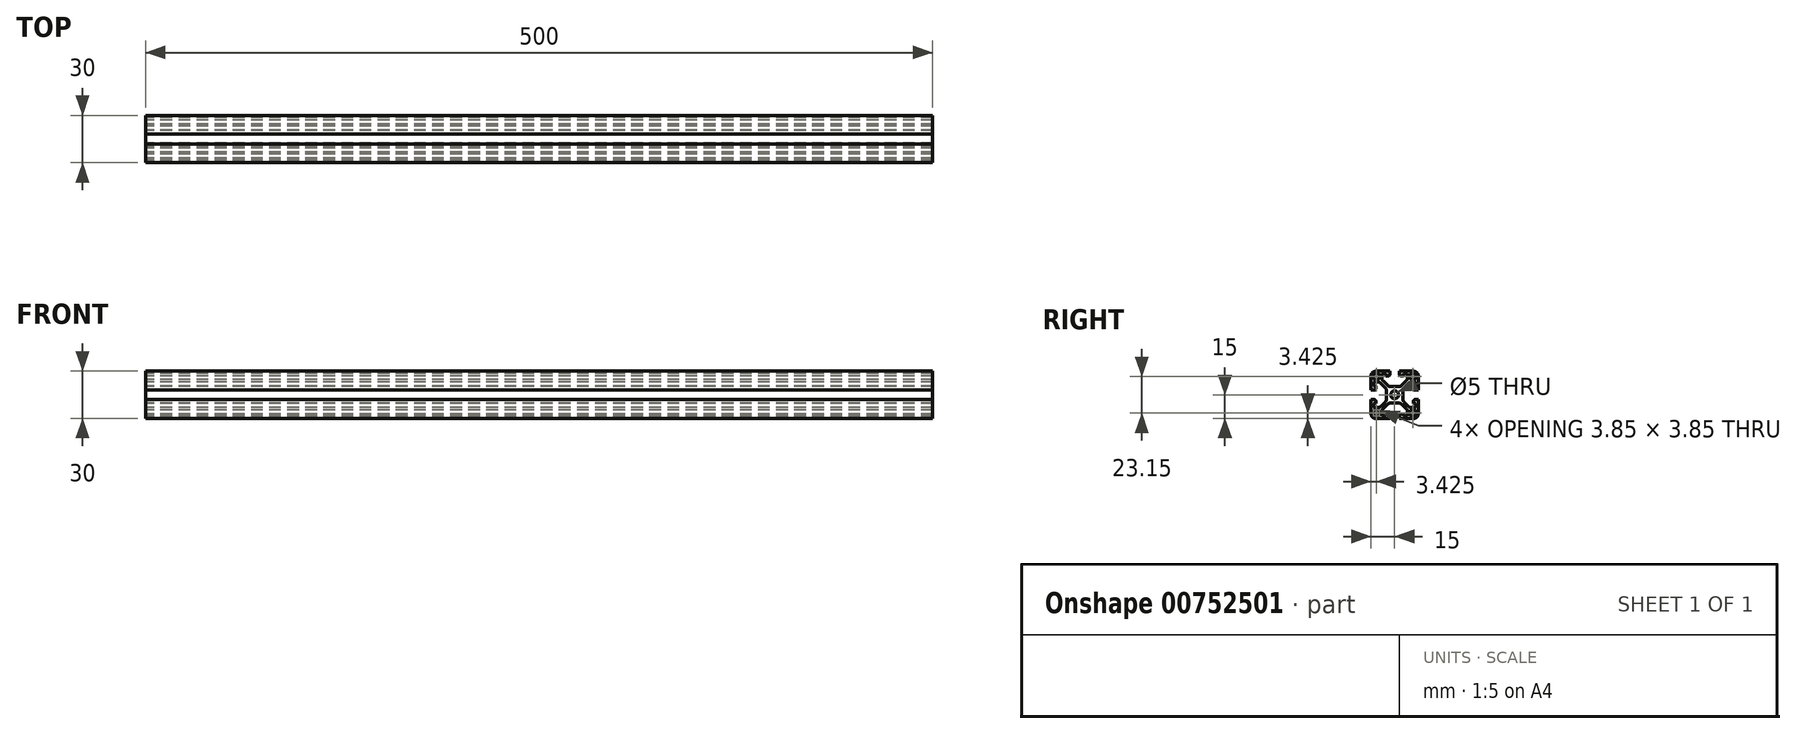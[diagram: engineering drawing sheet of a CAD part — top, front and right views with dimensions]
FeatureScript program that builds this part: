
annotation { "Feature Type Name" : "Feature", "Feature Type Description" : "" }
export const myFeature = defineFeature(function(context is Context, id is Id, definition is map)
    precondition{}
    {
        {
            var Q0;
            Q0=qCreatedBy(makeId("Right.planeOp"),FACE);
            var sketch = newSketch(context, id + "F0", { "sketchPlane" : qUnion([Q0])});
            skLineSegment(sketch, "E0.bottom", {"start": v(-12, 15) * mm, "end": v(-3.1, 15) * mm});
            skLineSegment(sketch, "E0.top", {"start": v(-12, -15) * mm, "end": v(-3.1, -15) * mm});
            skLineSegment(sketch, "E0.right", {"start": v(15, 12) * mm, "end": v(15, 3.1) * mm});
            skLineSegment(sketch, "E1", {"start": v(0, 31.7) * mm, "end": v(0, -24.01) * mm, "construction": true});
            skLineSegment(sketch, "E2", {"start": v(-29.71, 0) * mm, "end": v(21.95, 0) * mm, "construction": true});
            skLineSegment(sketch, "E3", {"start": v(-3.1, 15) * mm, "end": v(-3.1, 12.8) * mm});
            skLineSegment(sketch, "E4", {"start": v(-3.9, 12) * mm, "end": v(-5.6, 12) * mm});
            skLineSegment(sketch, "E5", {"start": v(-5.6, 12) * mm, "end": v(-5.6, 13.5) * mm});
            skLineSegment(sketch, "E6", {"start": v(-5.6, 13.5) * mm, "end": v(-8.15, 13.5) * mm});
            skLineSegment(sketch, "E7", {"start": v(-8.15, 13.5) * mm, "end": v(-8.15, 10.8) * mm});
            skLineSegment(sketch, "E8", {"start": v(-7.27, 8.68) * mm, "end": v(-4.72, 6.13) * mm});
            skLineSegment(sketch, "E9", {"start": v(-2.6, 5.25) * mm, "end": v(2.6, 5.25) * mm});
            skLineSegment(sketch, "E10", {"start": v(4.72, 6.13) * mm, "end": v(7.27, 8.68) * mm});
            skLineSegment(sketch, "E11", {"start": v(8.15, 10.8) * mm, "end": v(8.15, 13.5) * mm});
            skLineSegment(sketch, "E12", {"start": v(8.15, 13.5) * mm, "end": v(5.6, 13.5) * mm});
            skLineSegment(sketch, "E13", {"start": v(5.6, 13.5) * mm, "end": v(5.6, 12) * mm});
            skLineSegment(sketch, "E14", {"start": v(5.6, 12) * mm, "end": v(3.9, 12) * mm});
            skLineSegment(sketch, "E15", {"start": v(3.1, 12.8) * mm, "end": v(3.1, 15) * mm});
            skLineSegment(sketch, "E16.trimOffspring", {"start": v(3.1, 15) * mm, "end": v(12, 15) * mm});
            skLineSegment(sketch, "E17.bottom", {"start": v(-12, 13.5) * mm, "end": v(-9.65, 13.5) * mm});
            skLineSegment(sketch, "E17.top", {"start": v(-13.5, 9.65) * mm, "end": v(-9.65, 9.65) * mm});
            skLineSegment(sketch, "E17.left", {"start": v(-13.5, 12) * mm, "end": v(-13.5, 9.65) * mm});
            skLineSegment(sketch, "E17.right", {"start": v(-9.65, 13.5) * mm, "end": v(-9.65, 9.65) * mm});
            skPoint(sketch, "E18.visualSharp", {"position": v(-13.5, 13.5) * mm});
            skArc(sketch, "E18.filletArc", {"start": v(-12, 13.5) * mm, "mid": v(-13.06, 13.06) * mm, "end": v(-13.5, 12) * mm});
            skPoint(sketch, "E19.visualSharp", {"position": v(-15, 15) * mm});
            skArc(sketch, "E19.filletArc", {"start": v(-12, 15) * mm, "mid": v(-14.12, 14.12) * mm, "end": v(-15, 12) * mm});
            skPoint(sketch, "E20.visualSharp", {"position": v(-15, -15) * mm});
            skArc(sketch, "E20.filletArc", {"start": v(-15, -12) * mm, "mid": v(-14.12, -14.12) * mm, "end": v(-12, -15) * mm});
            skPoint(sketch, "E21.visualSharp", {"position": v(15, -15) * mm});
            skArc(sketch, "E21.filletArc", {"start": v(12, -15) * mm, "mid": v(14.12, -14.12) * mm, "end": v(15, -12) * mm});
            skPoint(sketch, "E22.visualSharp", {"position": v(15, 15) * mm});
            skArc(sketch, "E22.filletArc", {"start": v(15, 12) * mm, "mid": v(14.12, 14.12) * mm, "end": v(12, 15) * mm});
            skPoint(sketch, "E23.visualSharp", {"position": v(-8.15, 9.56) * mm});
            skArc(sketch, "E23.filletArc", {"start": v(-8.15, 10.8) * mm, "mid": v(-7.92, 9.66) * mm, "end": v(-7.27, 8.68) * mm});
            skPoint(sketch, "E24.visualSharp", {"position": v(-3.84, 5.25) * mm});
            skArc(sketch, "E24.filletArc", {"start": v(-4.72, 6.13) * mm, "mid": v(-3.74, 5.48) * mm, "end": v(-2.6, 5.25) * mm});
            skPoint(sketch, "E25.visualSharp", {"position": v(3.84, 5.25) * mm});
            skArc(sketch, "E25.filletArc", {"start": v(2.6, 5.25) * mm, "mid": v(3.74, 5.48) * mm, "end": v(4.72, 6.13) * mm});
            skPoint(sketch, "E26.visualSharp", {"position": v(8.15, 9.56) * mm});
            skArc(sketch, "E26.filletArc", {"start": v(7.27, 8.68) * mm, "mid": v(7.92, 9.66) * mm, "end": v(8.15, 10.8) * mm});
            skPoint(sketch, "E27.visualSharp", {"position": v(3.1, 12) * mm});
            skArc(sketch, "E27.filletArc", {"start": v(3.1, 12.8) * mm, "mid": v(3.33, 12.23) * mm, "end": v(3.9, 12) * mm});
            skPoint(sketch, "E28.visualSharp", {"position": v(-3.1, 12) * mm});
            skArc(sketch, "E28.filletArc", {"start": v(-3.9, 12) * mm, "mid": v(-3.33, 12.23) * mm, "end": v(-3.1, 12.8) * mm});
            skLineSegment(sketch, "E29.1.0", {"start": v(-5.25, -2.6) * mm, "end": v(-5.25, 2.6) * mm});
            skLineSegment(sketch, "E29.1.1", {"start": v(-12.8, 3.1) * mm, "end": v(-15, 3.1) * mm});
            skLineSegment(sketch, "E29.1.2", {"start": v(-6.13, 4.72) * mm, "end": v(-8.68, 7.27) * mm});
            skPoint(sketch, "E29.1.3", {"position": v(-12, -3.1) * mm});
            skLineSegment(sketch, "E29.1.4", {"start": v(-13.5, -5.6) * mm, "end": v(-13.5, -8.15) * mm});
            skPoint(sketch, "E29.1.5", {"position": v(-5.25, 3.84) * mm});
            skLineSegment(sketch, "E29.1.6", {"start": v(-13.5, -12) * mm, "end": v(-13.5, -9.65) * mm});
            skPoint(sketch, "E29.1.7", {"position": v(-5.25, -3.84) * mm});
            skLineSegment(sketch, "E29.1.8", {"start": v(-10.8, 8.15) * mm, "end": v(-13.5, 8.15) * mm});
            skLineSegment(sketch, "E29.1.9", {"start": v(-9.65, -13.5) * mm, "end": v(-9.65, -9.65) * mm});
            skLineSegment(sketch, "E29.1.10", {"start": v(-12, -13.5) * mm, "end": v(-9.65, -13.5) * mm});
            skLineSegment(sketch, "E29.1.11", {"start": v(-13.5, -8.15) * mm, "end": v(-10.8, -8.15) * mm});
            skLineSegment(sketch, "E29.1.12", {"start": v(-13.5, -9.65) * mm, "end": v(-9.65, -9.65) * mm});
            skPoint(sketch, "E29.1.13", {"position": v(-9.56, 8.15) * mm});
            skLineSegment(sketch, "E29.1.14", {"start": v(-8.68, -7.27) * mm, "end": v(-6.13, -4.72) * mm});
            skPoint(sketch, "E29.1.15", {"position": v(-12, 3.1) * mm});
            skPoint(sketch, "E29.1.16", {"position": v(-9.56, -8.15) * mm});
            skLineSegment(sketch, "E29.1.17", {"start": v(-15, -3.1) * mm, "end": v(-12.8, -3.1) * mm});
            skLineSegment(sketch, "E29.1.18", {"start": v(-13.5, 8.15) * mm, "end": v(-13.5, 5.6) * mm});
            skArc(sketch, "E29.1.19", {"start": v(-10.8, -8.15) * mm, "mid": v(-9.66, -7.92) * mm, "end": v(-8.68, -7.27) * mm});
            skArc(sketch, "E29.1.20", {"start": v(-6.13, -4.72) * mm, "mid": v(-5.48, -3.74) * mm, "end": v(-5.25, -2.6) * mm});
            skArc(sketch, "E29.1.21", {"start": v(-13.5, -12) * mm, "mid": v(-13.06, -13.06) * mm, "end": v(-12, -13.5) * mm});
            skArc(sketch, "E29.1.22", {"start": v(-8.68, 7.27) * mm, "mid": v(-9.66, 7.92) * mm, "end": v(-10.8, 8.15) * mm});
            skArc(sketch, "E29.1.23", {"start": v(-5.25, 2.6) * mm, "mid": v(-5.48, 3.74) * mm, "end": v(-6.13, 4.72) * mm});
            skLineSegment(sketch, "E29.1.24", {"start": v(-12, -5.6) * mm, "end": v(-13.5, -5.6) * mm});
            skLineSegment(sketch, "E29.1.25", {"start": v(-13.5, 5.6) * mm, "end": v(-12, 5.6) * mm});
            skLineSegment(sketch, "E29.1.26", {"start": v(-12, 5.6) * mm, "end": v(-12, 3.9) * mm});
            skLineSegment(sketch, "E29.1.27", {"start": v(-12, -3.9) * mm, "end": v(-12, -5.6) * mm});
            skArc(sketch, "E29.1.28", {"start": v(-12, -3.9) * mm, "mid": v(-12.23, -3.33) * mm, "end": v(-12.8, -3.1) * mm});
            skArc(sketch, "E29.1.29", {"start": v(-12.8, 3.1) * mm, "mid": v(-12.23, 3.33) * mm, "end": v(-12, 3.9) * mm});
            skLineSegment(sketch, "E29.2.0", {"start": v(2.6, -5.25) * mm, "end": v(-2.6, -5.25) * mm});
            skLineSegment(sketch, "E29.2.1", {"start": v(-3.1, -12.8) * mm, "end": v(-3.1, -15) * mm});
            skLineSegment(sketch, "E29.2.2", {"start": v(-4.72, -6.13) * mm, "end": v(-7.27, -8.68) * mm});
            skPoint(sketch, "E29.2.3", {"position": v(3.1, -12) * mm});
            skLineSegment(sketch, "E29.2.4", {"start": v(5.6, -13.5) * mm, "end": v(8.15, -13.5) * mm});
            skPoint(sketch, "E29.2.5", {"position": v(-3.84, -5.25) * mm});
            skLineSegment(sketch, "E29.2.6", {"start": v(12, -13.5) * mm, "end": v(9.65, -13.5) * mm});
            skPoint(sketch, "E29.2.7", {"position": v(3.84, -5.25) * mm});
            skLineSegment(sketch, "E29.2.8", {"start": v(-8.15, -10.8) * mm, "end": v(-8.15, -13.5) * mm});
            skLineSegment(sketch, "E29.2.9", {"start": v(13.5, -9.65) * mm, "end": v(9.65, -9.65) * mm});
            skLineSegment(sketch, "E29.2.10", {"start": v(13.5, -12) * mm, "end": v(13.5, -9.65) * mm});
            skLineSegment(sketch, "E29.2.11", {"start": v(8.15, -13.5) * mm, "end": v(8.15, -10.8) * mm});
            skLineSegment(sketch, "E29.2.12", {"start": v(9.65, -13.5) * mm, "end": v(9.65, -9.65) * mm});
            skPoint(sketch, "E29.2.13", {"position": v(-8.15, -9.56) * mm});
            skLineSegment(sketch, "E29.2.14", {"start": v(7.27, -8.68) * mm, "end": v(4.72, -6.13) * mm});
            skPoint(sketch, "E29.2.15", {"position": v(-3.1, -12) * mm});
            skPoint(sketch, "E29.2.16", {"position": v(8.15, -9.56) * mm});
            skLineSegment(sketch, "E29.2.17", {"start": v(3.1, -15) * mm, "end": v(3.1, -12.8) * mm});
            skLineSegment(sketch, "E29.2.18", {"start": v(-8.15, -13.5) * mm, "end": v(-5.6, -13.5) * mm});
            skArc(sketch, "E29.2.19", {"start": v(8.15, -10.8) * mm, "mid": v(7.92, -9.66) * mm, "end": v(7.27, -8.68) * mm});
            skArc(sketch, "E29.2.20", {"start": v(4.72, -6.13) * mm, "mid": v(3.74, -5.48) * mm, "end": v(2.6, -5.25) * mm});
            skArc(sketch, "E29.2.21", {"start": v(12, -13.5) * mm, "mid": v(13.06, -13.06) * mm, "end": v(13.5, -12) * mm});
            skArc(sketch, "E29.2.22", {"start": v(-7.27, -8.68) * mm, "mid": v(-7.92, -9.66) * mm, "end": v(-8.15, -10.8) * mm});
            skArc(sketch, "E29.2.23", {"start": v(-2.6, -5.25) * mm, "mid": v(-3.74, -5.48) * mm, "end": v(-4.72, -6.13) * mm});
            skLineSegment(sketch, "E29.2.24", {"start": v(5.6, -12) * mm, "end": v(5.6, -13.5) * mm});
            skLineSegment(sketch, "E29.2.25", {"start": v(-5.6, -13.5) * mm, "end": v(-5.6, -12) * mm});
            skLineSegment(sketch, "E29.2.26", {"start": v(-5.6, -12) * mm, "end": v(-3.9, -12) * mm});
            skLineSegment(sketch, "E29.2.27", {"start": v(3.9, -12) * mm, "end": v(5.6, -12) * mm});
            skArc(sketch, "E29.2.28", {"start": v(3.9, -12) * mm, "mid": v(3.33, -12.23) * mm, "end": v(3.1, -12.8) * mm});
            skArc(sketch, "E29.2.29", {"start": v(-3.1, -12.8) * mm, "mid": v(-3.33, -12.23) * mm, "end": v(-3.9, -12) * mm});
            skLineSegment(sketch, "E29.3.0", {"start": v(5.25, 2.6) * mm, "end": v(5.25, -2.6) * mm});
            skLineSegment(sketch, "E29.3.1", {"start": v(12.8, -3.1) * mm, "end": v(15, -3.1) * mm});
            skLineSegment(sketch, "E29.3.2", {"start": v(6.13, -4.72) * mm, "end": v(8.68, -7.27) * mm});
            skPoint(sketch, "E29.3.3", {"position": v(12, 3.1) * mm});
            skLineSegment(sketch, "E29.3.4", {"start": v(13.5, 5.6) * mm, "end": v(13.5, 8.15) * mm});
            skPoint(sketch, "E29.3.5", {"position": v(5.25, -3.84) * mm});
            skLineSegment(sketch, "E29.3.6", {"start": v(13.5, 12) * mm, "end": v(13.5, 9.65) * mm});
            skPoint(sketch, "E29.3.7", {"position": v(5.25, 3.84) * mm});
            skLineSegment(sketch, "E29.3.8", {"start": v(10.8, -8.15) * mm, "end": v(13.5, -8.15) * mm});
            skLineSegment(sketch, "E29.3.9", {"start": v(9.65, 13.5) * mm, "end": v(9.65, 9.65) * mm});
            skLineSegment(sketch, "E29.3.10", {"start": v(12, 13.5) * mm, "end": v(9.65, 13.5) * mm});
            skLineSegment(sketch, "E29.3.11", {"start": v(13.5, 8.15) * mm, "end": v(10.8, 8.15) * mm});
            skLineSegment(sketch, "E29.3.12", {"start": v(13.5, 9.65) * mm, "end": v(9.65, 9.65) * mm});
            skPoint(sketch, "E29.3.13", {"position": v(9.56, -8.15) * mm});
            skLineSegment(sketch, "E29.3.14", {"start": v(8.68, 7.27) * mm, "end": v(6.13, 4.72) * mm});
            skPoint(sketch, "E29.3.15", {"position": v(12, -3.1) * mm});
            skPoint(sketch, "E29.3.16", {"position": v(9.56, 8.15) * mm});
            skLineSegment(sketch, "E29.3.17", {"start": v(15, 3.1) * mm, "end": v(12.8, 3.1) * mm});
            skLineSegment(sketch, "E29.3.18", {"start": v(13.5, -8.15) * mm, "end": v(13.5, -5.6) * mm});
            skArc(sketch, "E29.3.19", {"start": v(10.8, 8.15) * mm, "mid": v(9.66, 7.92) * mm, "end": v(8.68, 7.27) * mm});
            skArc(sketch, "E29.3.20", {"start": v(6.13, 4.72) * mm, "mid": v(5.48, 3.74) * mm, "end": v(5.25, 2.6) * mm});
            skArc(sketch, "E29.3.21", {"start": v(13.5, 12) * mm, "mid": v(13.06, 13.06) * mm, "end": v(12, 13.5) * mm});
            skArc(sketch, "E29.3.22", {"start": v(8.68, -7.27) * mm, "mid": v(9.66, -7.92) * mm, "end": v(10.8, -8.15) * mm});
            skArc(sketch, "E29.3.23", {"start": v(5.25, -2.6) * mm, "mid": v(5.48, -3.74) * mm, "end": v(6.13, -4.72) * mm});
            skLineSegment(sketch, "E29.3.24", {"start": v(12, 5.6) * mm, "end": v(13.5, 5.6) * mm});
            skLineSegment(sketch, "E29.3.25", {"start": v(13.5, -5.6) * mm, "end": v(12, -5.6) * mm});
            skLineSegment(sketch, "E29.3.26", {"start": v(12, -5.6) * mm, "end": v(12, -3.9) * mm});
            skLineSegment(sketch, "E29.3.27", {"start": v(12, 3.9) * mm, "end": v(12, 5.6) * mm});
            skArc(sketch, "E29.3.28", {"start": v(12, 3.9) * mm, "mid": v(12.23, 3.33) * mm, "end": v(12.8, 3.1) * mm});
            skArc(sketch, "E29.3.29", {"start": v(12.8, -3.1) * mm, "mid": v(12.23, -3.33) * mm, "end": v(12, -3.9) * mm});
            skPoint(sketch, "E29.center", {"position": v(0, 0) * mm});
            skLineSegment(sketch, "E30.trimOffspring", {"start": v(-15, -3.1) * mm, "end": v(-15, -12) * mm});
            skLineSegment(sketch, "E31.trimOffspring", {"start": v(15, -3.1) * mm, "end": v(15, -12) * mm});
            skLineSegment(sketch, "E32.trimOffspring", {"start": v(3.1, -15) * mm, "end": v(12, -15) * mm});
            skLineSegment(sketch, "E33", {"start": v(-15, 12) * mm, "end": v(-15, 3.1) * mm});
            skCircle(sketch, "E34", {"center": v(0, 0) * mm, "radius": 2.5 * mm});
            skSolve(sketch);
        }
        {
            var Q0;
            Q0 = qSketchRegion(id + "F0", true);
            extrude(context, id + "F1", {"entities" : qUnion([Q0]), "depth" : 500 * mm, "offsetDistance" : 25 * mm});
        }
    });
